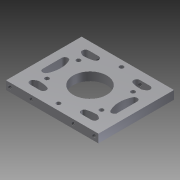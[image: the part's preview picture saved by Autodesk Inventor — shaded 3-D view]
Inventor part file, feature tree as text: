
AUTODESK INVENTOR PART (.ipt)
format: ipt  version: 2012 (Build 160160000, 160)  size: 306,176 bytes
history: native  units: in
note: dims shown in document units (in); Inventor stores cm internally (conversion verified against a paired STEP export)
features: thread x6, sketch x5, hole x4, extrude x3, fillet x2, plane x1, projected_geometry x1
ambient origin geometry x8: Origin, YZ Plane, XZ Plane, XY Plane, X Axis, Y Axis, Z Axis, Center Point
bodies: Solid1 (feature_tree)
feature tree (22):
  sketch  "Sketch1"  dims[d0=1.375in d1=2.75in]
  extrude  "Extrusion1"  Depth=2.75in
  hole  "Hole6"  [1 undecoded]
  plane  "Work Plane5"
  extrude  "Extrusion6"  Depth=0.25in TaperAngle=0.0deg
  fillet  "Fillet1"  Radius=1.875in
  sketch  "Sketch13"  dims[d4=1.0in d6=0.25in d7=0.0in d139=1.875in]
  sketch  "Sketch14"  dims[d140=2.3622in d142=360.0deg]
  hole  "Hole8"  [1 undecoded]
  thread  "Thread9"  [1 undecoded]
  thread  "Thread11"  [1 undecoded]
  hole  "Hole11"  [1 undecoded]
  hole  "Hole12"  [1 undecoded]
  thread  "Thread13"  [1 undecoded]
  thread  "Thread14"  [1 undecoded]
  thread  "Thread15"  [1 undecoded]
  thread  "Thread16"  [1 undecoded]
  extrude  "Extrusion8"  Depth=0.25in
  fillet  "Fillet5"  Radius=0.125in
  sketch  "Sketch12"  dims[d2=2.25in d3=1.125in]
  projected_geometry  "Projected Loop1"
  sketch  "Sketch16"  dims[d144=0.125in d145=0.75in d146=0.1875in d147=0.25in d148=0.5635in d149=1.0in d150=0.8108in d160=-0.125in d161=0.1875in d162=1.0in d168=0.25in d169=0.25in d170=0.25in d171=0.125in d173=0.125in d174=0.25in d175=0.25in d176=0.125in d177=0.25in d178=0.125in d179=0.1875in d180=1.0in d181=0.1875in d182=1.0in d183=0.1875in d184=1.0in d185=0.1875in d186=0.1875in d187=1.0in d188=1.0in d189=1.0in d190=0.0in d191=0.0625in d192=0.25in d193=0.25in d194=0.25in d195=0.25in d197=0.1875in d198=0.75in d199=0.125in d200=0.125in d201=0.125in d202=0.125in d203=0.125in d204=0.125in d205=0.125in d206=0.125in d211=0.125in d212=0.125in d213=0.125in d214=0.125in d215=0.106in d216=0.75in d217=0.375in d218=0.25in d219=0.5635in d220=1.0in d221=0.8108in d240=1.0in d241=0.0in d244=1.0in d245=0.0in d251=0.7504in d252=0.75in d253=0.106in d254=0.75in d255=0.375in d256=0.25in d257=0.5635in d258=0.3in d259=0.8108in d260=0.75in d261=0.75in d262=0.106in d263=0.75in d264=0.375in d265=0.25in d266=0.5635in d267=0.3in d268=0.8108in d269=1.0in d270=0.0in d271=1.0in d272=0.0in d273=1.0in d274=0.0in d275=1.0in d276=0.0in d277=90.0deg d278=45.0deg d289=0.25in d290=0.25in d291=1.0in d292=0.0in d293=0.0938in d294=0.25in d295=0.125in d296=0.25in d297=0.125in d45=1.0in d46=1.0in d132=1.0in d133=1.0in]
note: 10 required parameter values undecoded (feature->parameter linkage not recoverable at this tier; creation-order binding heuristic only, values carry confidence <= 0.55)
